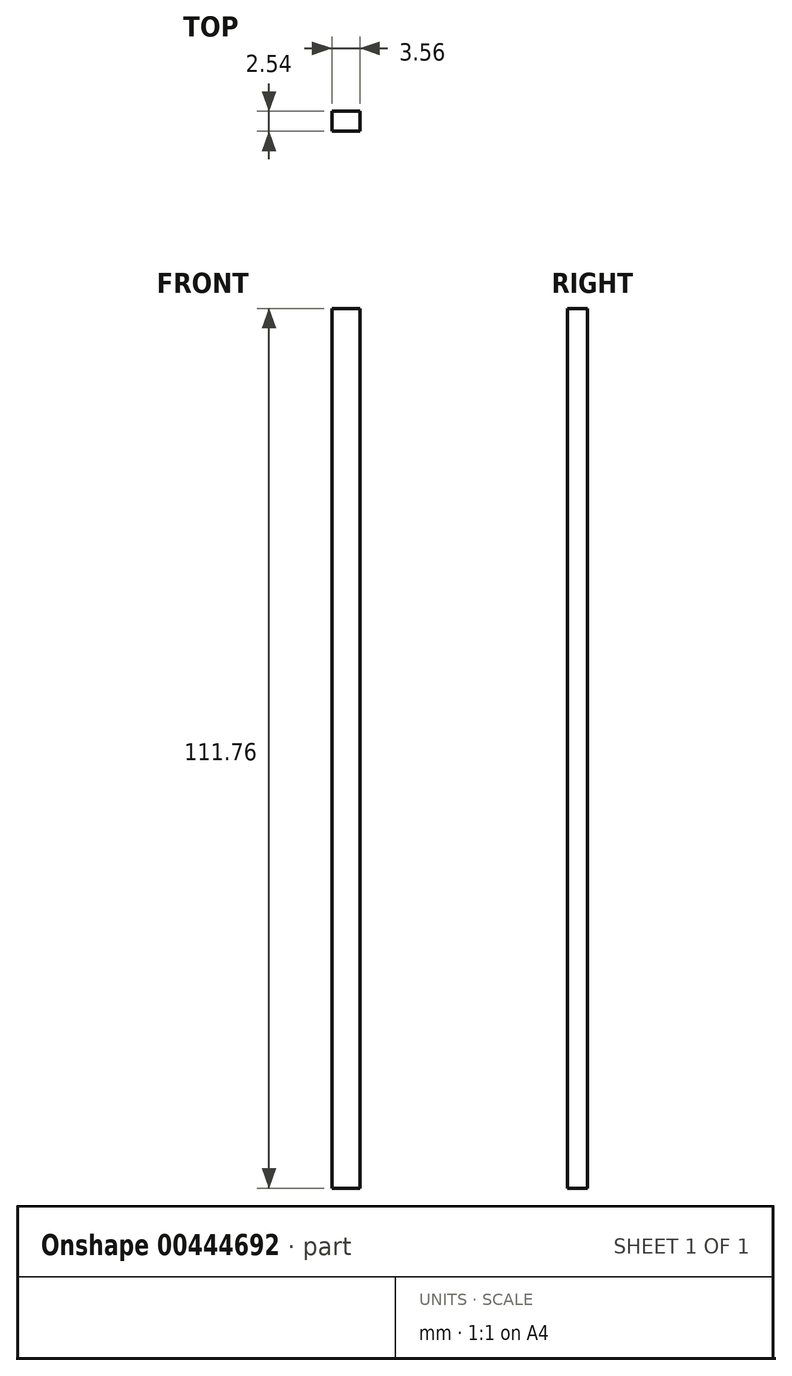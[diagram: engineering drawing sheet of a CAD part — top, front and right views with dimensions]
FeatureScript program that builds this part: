
annotation { "Feature Type Name" : "Feature", "Feature Type Description" : "" }
export const myFeature = defineFeature(function(context is Context, id is Id, definition is map)
    precondition{}
    {
        {
            var Q0;
            Q0=qCreatedBy(makeId("Front.planeOp"),FACE);
            var sketch = newSketch(context, id + "F0", { "sketchPlane" : qUnion([Q0])});
            skLineSegment(sketch, "E0.bottom", {"start": v(-28.2, 70.03) * mm, "end": v(-31.76, 70.03) * mm});
            skLineSegment(sketch, "E0.top", {"start": v(-28.2, -41.73) * mm, "end": v(-31.76, -41.73) * mm});
            skLineSegment(sketch, "E0.left", {"start": v(-28.2, 70.03) * mm, "end": v(-28.2, -41.73) * mm});
            skLineSegment(sketch, "E0.right", {"start": v(-31.76, 70.03) * mm, "end": v(-31.76, -41.73) * mm});
            skSolve(sketch);
        }
        {
            var Q0;
            Q0 = qSketchRegion(id + "F0", true);
            extrude(context, id + "F1", {"entities" : qUnion([Q0]), "depth" : 2.54 * mm});
        }
    });
